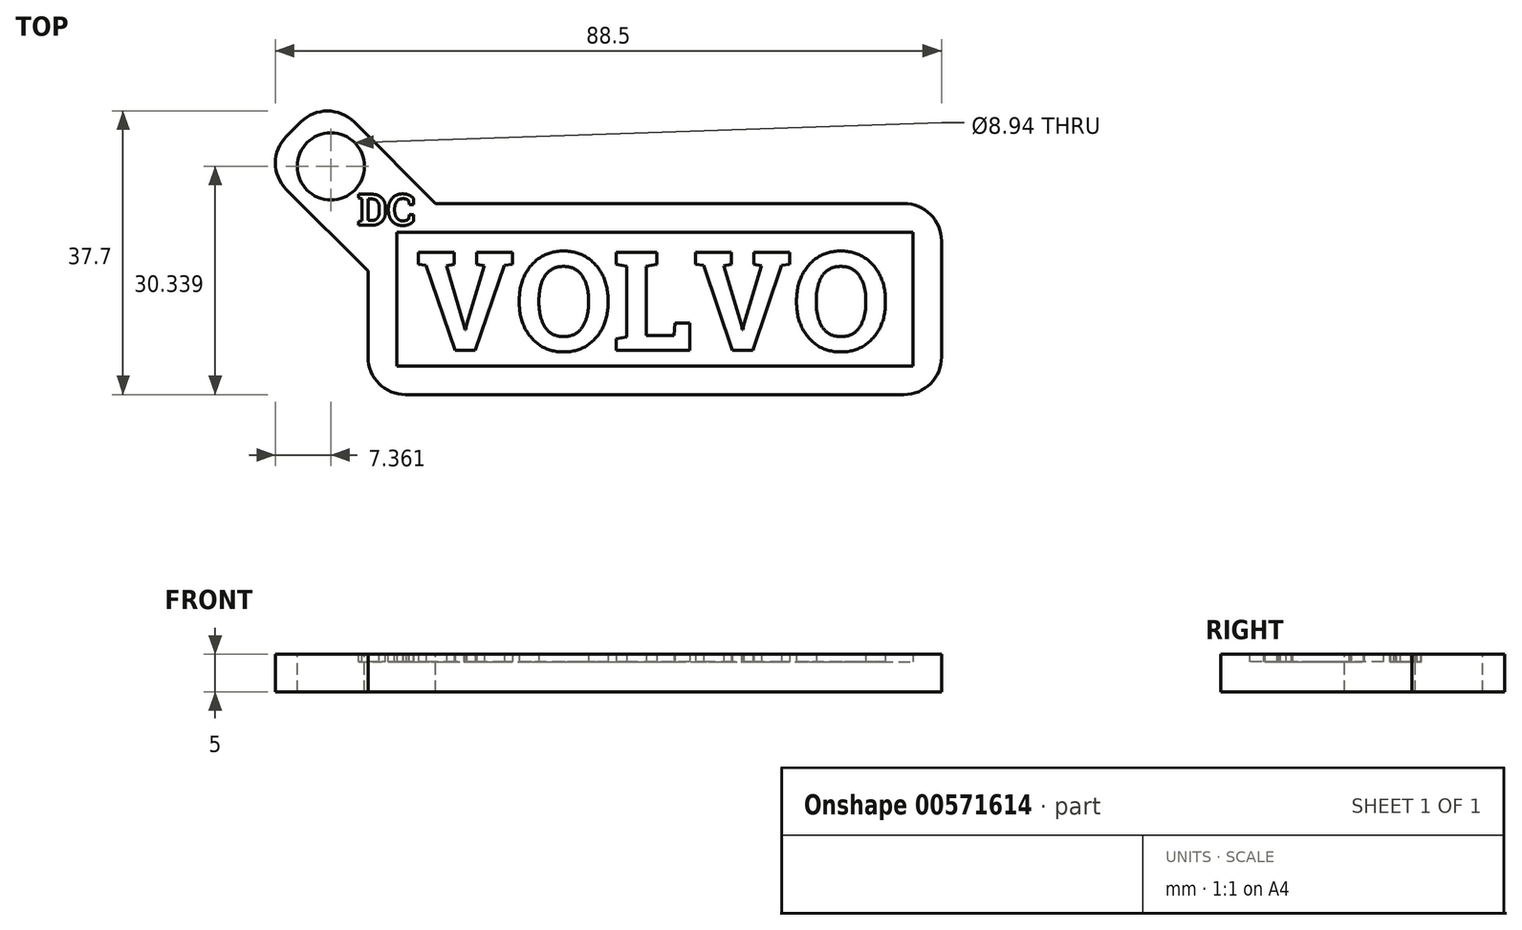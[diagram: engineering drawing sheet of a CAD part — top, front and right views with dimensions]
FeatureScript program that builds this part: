
annotation { "Feature Type Name" : "Feature", "Feature Type Description" : "" }
export const myFeature = defineFeature(function(context is Context, id is Id, definition is map)
    precondition{}
    {
        {
            var Q0;
            Q0=qCreatedBy(makeId("Top.planeOp"),FACE);
            var sketch = newSketch(context, id + "F0", { "sketchPlane" : qUnion([Q0])});
            skLineSegment(sketch, "E0.bottom", {"start": v(38.1, 12.7) * mm, "end": v(-38.1, 12.7) * mm});
            skLineSegment(sketch, "E0.top", {"start": v(38.1, -12.7) * mm, "end": v(-38.1, -12.7) * mm});
            skLineSegment(sketch, "E0.left", {"start": v(38.1, 12.7) * mm, "end": v(38.1, -12.7) * mm});
            skLineSegment(sketch, "E0.right", {"start": v(-38.1, 12.7) * mm, "end": v(-38.1, -12.7) * mm});
            skPoint(sketch, "E0.middle", {"position": v(0, 0) * mm});
            skSolve(sketch);
        }
        {
            var Q0;
            Q0 = qSketchRegion(id + "F0", true);
            extrude(context, id + "F1", {"entities" : qUnion([Q0]), "oppositeDirection" : true, "depth" : 4 * mm, "offsetDistance" : 25 * mm});
        }
        {
            var Q0;
            Q0=makeQuery(id+"F1.opExtrude","CAP_FACE",FACE,{"disambiguationData":[OSD([sQuery(id+"F0.wireOp",EDGE,"E0.bottom"),sQuery(id+"F0.wireOp",EDGE,"E0.top"),sQuery(id+"F0.wireOp",EDGE,"E0.left"),sQuery(id+"F0.wireOp",EDGE,"E0.right")])],"isStart":true});
            var sketch = newSketch(context, id + "F2", { "sketchPlane" : qUnion([Q0])});
            skLineSegment(sketch, "E1.bottom", {"start": v(-38.1, 12.7) * mm, "end": v(-34.3, 12.7) * mm});
            skLineSegment(sketch, "E1.top", {"start": v(-38.1, -12.7) * mm, "end": v(-34.3, -12.7) * mm});
            skLineSegment(sketch, "E1.left", {"start": v(-38.1, 12.7) * mm, "end": v(-38.1, -12.7) * mm});
            skLineSegment(sketch, "E1.right", {"start": v(-34.3, 12.7) * mm, "end": v(-34.3, -12.7) * mm});
            skLineSegment(sketch, "E2.bottom", {"start": v(-34.3, -8.9) * mm, "end": v(38.1, -8.9) * mm});
            skLineSegment(sketch, "E2.top", {"start": v(-34.3, -12.7) * mm, "end": v(38.1, -12.7) * mm});
            skLineSegment(sketch, "E2.left", {"start": v(-34.3, -8.9) * mm, "end": v(-34.3, -12.7) * mm});
            skLineSegment(sketch, "E2.right", {"start": v(38.1, -8.9) * mm, "end": v(38.1, -12.7) * mm});
            skLineSegment(sketch, "E3.bottom", {"start": v(38.1, 12.7) * mm, "end": v(34.3, 12.7) * mm});
            skLineSegment(sketch, "E3.top", {"start": v(38.1, -8.9) * mm, "end": v(34.3, -8.9) * mm});
            skLineSegment(sketch, "E3.left", {"start": v(38.1, 12.7) * mm, "end": v(38.1, -8.9) * mm});
            skLineSegment(sketch, "E3.right", {"start": v(34.3, 12.7) * mm, "end": v(34.3, -8.9) * mm});
            skLineSegment(sketch, "E4.bottom", {"start": v(-34.3, 12.7) * mm, "end": v(34.29, 12.7) * mm});
            skLineSegment(sketch, "E4.top", {"start": v(-34.3, 8.9) * mm, "end": v(34.3, 8.9) * mm});
            skLineSegment(sketch, "E4.left", {"start": v(-34.3, 12.7) * mm, "end": v(-34.3, 8.9) * mm});
            skLineSegment(sketch, "E4.right", {"start": v(34.3, 12.7) * mm, "end": v(34.3, 8.9) * mm});
            skSolve(sketch);
        }
        {
            var Q0;
            Q0 = qSketchRegion(id + "F2", true);
            extrude(context, id + "F3", {"entities" : qUnion([Q0]), "operationType" : NewBodyOperationType.ADD, "depth" : 1 * mm, "offsetDistance" : 25 * mm});
        }
        {
            var Q0;
            Q0=makeQuery(id+"F3.opExtrude","CAP_FACE",FACE,{"disambiguationData":[OSD([sQuery(id+"F2.wireOp",EDGE,"E1.bottom"),sQuery(id+"F2.wireOp",EDGE,"E1.top"),sQuery(id+"F2.wireOp",EDGE,"E1.left"),sQuery(id+"F2.wireOp",EDGE,"E1.right"),sQuery(id+"F2.wireOp",EDGE,"E2.bottom"),sQuery(id+"F2.wireOp",EDGE,"E2.top"),sQuery(id+"F2.wireOp",EDGE,"E2.right"),sQuery(id+"F2.wireOp",EDGE,"E3.bottom"),sQuery(id+"F2.wireOp",EDGE,"E3.left"),sQuery(id+"F2.wireOp",EDGE,"E3.right"),sQuery(id+"F2.wireOp",EDGE,"E4.bottom"),sQuery(id+"F2.wireOp",EDGE,"E4.top")])],"isStart":false});
            var sketch = newSketch(context, id + "F4", { "sketchPlane" : qUnion([Q0])});
            skLineSegment(sketch, "E5", {"start": v(-29.12, 12.7) * mm, "end": v(-38.1, 3.72) * mm, "construction": true});
            skLineSegment(sketch, "E6", {"start": v(-29.12, 12.7) * mm, "end": v(-43.49, 27.07) * mm});
            skLineSegment(sketch, "E7", {"start": v(-38.1, 3.72) * mm, "end": v(-52.47, 18.09) * mm});
            skLineSegment(sketch, "E8", {"start": v(-52.47, 18.09) * mm, "end": v(-43.49, 27.07) * mm});
            skLineSegment(sketch, "E9", {"start": v(-47.98, 22.58) * mm, "end": v(-38.1, 12.7) * mm, "construction": true});
            skLineSegment(sketch, "E10", {"start": v(-38.1, 12.7) * mm, "end": v(-38.1, 21.68) * mm, "construction": true});
            skLineSegment(sketch, "E11", {"start": v(-38.1, 21.68) * mm, "end": v(-47.08, 12.7) * mm, "construction": true});
            skLineSegment(sketch, "E12", {"start": v(-47.08, 12.7) * mm, "end": v(-47.98, 22.58) * mm, "construction": true});
            skLineSegment(sketch, "E13", {"start": v(-38.1, 21.68) * mm, "end": v(-47.98, 22.58) * mm, "construction": true});
            skLineSegment(sketch, "E14", {"start": v(-47.08, 12.7) * mm, "end": v(-38.1, 12.7) * mm, "construction": true});
            skCircle(sketch, "E15", {"center": v(-43.04, 17.64) * mm, "radius": 4.47 * mm});
            skSolve(sketch);
        }
        {
            var Q0;
            {var subQ4=sQuery(id+"F4.wireOp",EDGE,"E6");Q0=makeQuery(id+"F4.imprint","IMPRINT",FACE,{"disambiguationData":[TD([[makeQuery(id+"F4.imprint","IMPRINT",EDGE,{"derivedFrom":subQ4}),1.0]])]});}
            extrude(context, id + "F5", {"entities" : qUnion([Q0]), "operationType" : NewBodyOperationType.ADD, "oppositeDirection" : true, "depth" : 5 * mm, "offsetDistance" : 25 * mm});
        }
        {
            var Q0;
            Q0=makeQuery(id+"F1.opExtrude","CAP_FACE",FACE,{"disambiguationData":[OSD([sQuery(id+"F0.wireOp",EDGE,"E0.bottom"),sQuery(id+"F0.wireOp",EDGE,"E0.top"),sQuery(id+"F0.wireOp",EDGE,"E0.left"),sQuery(id+"F0.wireOp",EDGE,"E0.right")])],"isStart":true});
            var sketch = newSketch(context, id + "F6", { "sketchPlane" : qUnion([Q0])});
            skText(sketch, "E16", { "text": "VOLVO", "fontName": "RobotoSlab-Bold.ttf"});
            const initialGuessF6  = {"E16": [-0.03175, -0.00684, 1, 0, 0.0132]};
            skSetInitialGuess(sketch, initialGuessF6);
            skSolve(sketch);
        }
        {
            var Q0;
            Q0 = qSketchRegion(id + "F6", true);
            extrude(context, id + "F7", {"entities" : qUnion([Q0]), "operationType" : NewBodyOperationType.ADD, "depth" : 1 * mm, "offsetDistance" : 25.4 * mm});
        }
        {
            var Q0;
            {var subQ0=sQuery(id+"F2.wireOp",EDGE,"E4.bottom");var subQ1=sQuery(id+"F2.wireOp",EDGE,"E3.bottom");var subQ2=sQuery(id+"F2.wireOp",EDGE,"E1.left");var subQ3=sQuery(id+"F2.wireOp",EDGE,"E1.bottom");Q0=makeQuery(id+"F5.boolean.opBoolean","MERGE",FACE,{"derivedFrom":[makeQuery(id+"F3.opExtrude","CAP_FACE",FACE,{"disambiguationData":[OSD([subQ3,sQuery(id+"F2.wireOp",EDGE,"E1.top"),subQ2,sQuery(id+"F2.wireOp",EDGE,"E1.right"),sQuery(id+"F2.wireOp",EDGE,"E2.bottom"),sQuery(id+"F2.wireOp",EDGE,"E2.top"),sQuery(id+"F2.wireOp",EDGE,"E2.right"),subQ1,sQuery(id+"F2.wireOp",EDGE,"E3.left"),sQuery(id+"F2.wireOp",EDGE,"E3.right"),subQ0,sQuery(id+"F2.wireOp",EDGE,"E4.top")])],"isStart":false}),makeQuery(id+"F5.opExtrude","CAP_FACE",FACE,{"disambiguationData":[OSD([subQ3,subQ2,subQ1,subQ0,sQuery(id+"F4.wireOp",EDGE,"E6"),sQuery(id+"F4.wireOp",EDGE,"E7"),sQuery(id+"F4.wireOp",EDGE,"E8"),sQuery(id+"F4.wireOp",EDGE,"E15")])],"isStart":true})]});}
            var sketch = newSketch(context, id + "F8", { "sketchPlane" : qUnion([Q0])});
            skText(sketch, "E17", { "text": "DC", "fontName": "RobotoSlab-Bold.ttf"});
            const initialGuessF8  = {"E17": [-0.03952, 0.00982, 1, 0, 0.00416]};
            skSetInitialGuess(sketch, initialGuessF8);
            skSolve(sketch);
        }
        {
            var Q0;
            Q0 = qSketchRegion(id + "F8", true);
            extrude(context, id + "F9", {"entities" : qUnion([Q0]), "operationType" : NewBodyOperationType.ADD, "oppositeDirection" : true, "depth" : 1 * mm, "offsetDistance" : 25 * mm});
        }
        {
            var Q0;
            Q0 = qSketchRegion(id + "F8", true);
            extrude(context, id + "F10", {"entities" : qUnion([Q0]), "operationType" : NewBodyOperationType.REMOVE, "oppositeDirection" : true, "depth" : 1 * mm, "offsetDistance" : 25 * mm});
        }
        {
            var Q0;
            Q0=makeQuery(id+"F5.opExtrude","SWEPT_EDGE",EDGE,{"disambiguationData":[OSD([sQuery(id+"F4.wireOp",EDGE,"E6"),sQuery(id+"F4.wireOp",EDGE,"E8")])]});
            var Q1;
            Q1=makeQuery(id+"F5.opExtrude","SWEPT_EDGE",EDGE,{"disambiguationData":[OSD([sQuery(id+"F4.wireOp",EDGE,"E7"),sQuery(id+"F4.wireOp",EDGE,"E8")])]});
            var Q2;
            Q2=makeQuery(id+"F3.boolean.opBoolean","MERGE",EDGE,{"derivedFrom":[makeQuery(id+"F1.opExtrude","SWEPT_EDGE",EDGE,{"disambiguationData":[OSD([sQuery(id+"F0.wireOp",EDGE,"E0.bottom"),sQuery(id+"F0.wireOp",EDGE,"E0.left")])]}),makeQuery(id+"F3.opExtrude","SWEPT_EDGE",EDGE,{"disambiguationData":[OSD([sQuery(id+"F2.wireOp",EDGE,"E3.bottom"),sQuery(id+"F2.wireOp",EDGE,"E3.left")])]})]});
            var Q3;
            Q3=makeQuery(id+"F3.boolean.opBoolean","MERGE",EDGE,{"derivedFrom":[makeQuery(id+"F1.opExtrude","SWEPT_EDGE",EDGE,{"disambiguationData":[OSD([sQuery(id+"F0.wireOp",EDGE,"E0.top"),sQuery(id+"F0.wireOp",EDGE,"E0.left")])]}),makeQuery(id+"F3.opExtrude","SWEPT_EDGE",EDGE,{"disambiguationData":[OSD([sQuery(id+"F2.wireOp",EDGE,"E2.top"),sQuery(id+"F2.wireOp",EDGE,"E2.right")])]})]});
            var Q4;
            Q4=makeQuery(id+"F3.boolean.opBoolean","MERGE",EDGE,{"derivedFrom":[makeQuery(id+"F1.opExtrude","SWEPT_EDGE",EDGE,{"disambiguationData":[OSD([sQuery(id+"F0.wireOp",EDGE,"E0.top"),sQuery(id+"F0.wireOp",EDGE,"E0.right")])]}),makeQuery(id+"F3.opExtrude","SWEPT_EDGE",EDGE,{"disambiguationData":[OSD([sQuery(id+"F2.wireOp",EDGE,"E1.top"),sQuery(id+"F2.wireOp",EDGE,"E1.left")])]})]});
            var Q5;
            Q5=makeQuery(id+"F5.opExtrude","SWEPT_EDGE",EDGE,{"disambiguationData":[OSD([sQuery(id+"F2.wireOp",EDGE,"E1.bottom"),sQuery(id+"F2.wireOp",EDGE,"E3.bottom"),sQuery(id+"F2.wireOp",EDGE,"E4.bottom"),sQuery(id+"F4.wireOp",EDGE,"E6")])]});
            var Q6;
            Q6=makeQuery(id+"F5.opExtrude","SWEPT_EDGE",EDGE,{"disambiguationData":[OSD([sQuery(id+"F2.wireOp",EDGE,"E1.left"),sQuery(id+"F4.wireOp",EDGE,"E7")])]});
            fillet(context, id + "F11", {"entities" : qUnion([Q0, Q1, Q2, Q3, Q4, Q5, Q6]), "radius" : 5 * mm, "tangentPropagation" : true, "allowEdgeOverflow" : false});
        }
    });
